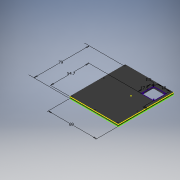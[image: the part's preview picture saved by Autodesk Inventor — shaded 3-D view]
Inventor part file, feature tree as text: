
AUTODESK INVENTOR PART (.ipt)
format: ipt  version: 2019.4 (Build 234330000, 330)  size: 154,624 bytes
history: native  units: mm
features: sketch x3, hole x3, extrude x2, pattern_linear x1
ambient origin geometry x8: Origin, YZ Plane, XZ Plane, XY Plane, X Axis, Y Axis, Z Axis, Center Point
bodies: Solid1 (feature_tree)
feature tree (9):
  extrude  "Extrusion1"  Depth=79.0mm
  sketch  "Sketch2"  dims[d2=2.5mm d3=0.0mm d4=2.0mm]
  hole  "Hole1"  [1 undecoded]
  pattern_linear  "Rectangular Pattern1"  Count1=2 Spacing1=65.0mm
  extrude  "Extrusion2"  Depth=1.25mm
  hole  "Hole2"  [1 undecoded]
  hole  "Hole3"  [1 undecoded]
  sketch  "Sketch1"  dims[d0=69.0mm d1=79.0mm]
  sketch  "Sketch3"  dims[d5=2.0mm d6=2.3mm d7=4.369mm d8=3.3mm d9=1.25mm d10=90.0deg d11=8.0mm d12=20.594885mm d13=20.0mm d15=65.0mm d16=20.0mm d18=75.0mm d19=54.7mm d20=4.0mm d21=18.0mm d22=17.5mm d23=2.5mm d24=0.0mm d25=1.5mm d26=2.0mm d27=2.0mm d28=32.0mm d29=30.0mm d30=2.3mm d31=4.369mm d32=3.3mm d33=1.25mm d34=90.0deg d35=8.0mm d36=20.594885mm d37=2.0mm d38=2.0mm d39=34.5mm d40=34.5mm d41=2.3mm d42=4.369mm d43=3.3mm d44=1.25mm d45=90.0deg d46=8.0mm d47=20.594885mm]
note: 3 required parameter values undecoded (feature->parameter linkage not recoverable at this tier; creation-order binding heuristic only, values carry confidence <= 0.55)
